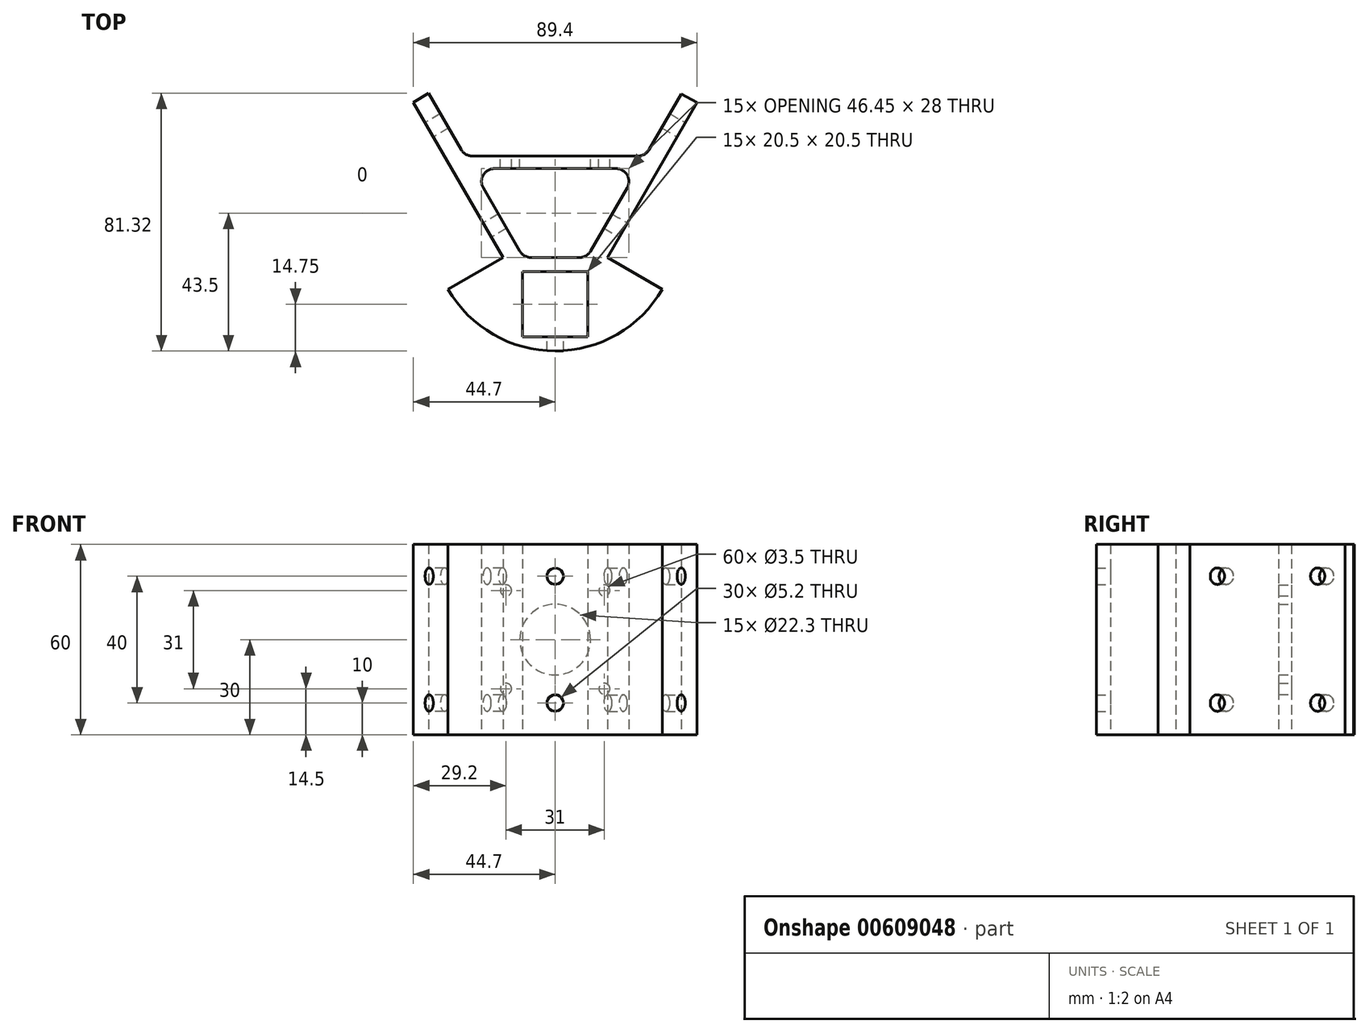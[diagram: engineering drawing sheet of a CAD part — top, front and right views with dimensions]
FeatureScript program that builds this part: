
annotation { "Feature Type Name" : "Feature", "Feature Type Description" : "" }
export const myFeature = defineFeature(function(context is Context, id is Id, definition is map)
    precondition{}
    {
        {
            var Q0;
            Q0=qCreatedBy(makeId("Top.planeOp"),FACE);
            var sketch = newSketch(context, id + "F0", { "sketchPlane" : qUnion([Q0])});
            skArc(sketch, "E0", {"start": v(-33.77, -19.5) * mm, "mid": v(0, -39) * mm, "end": v(33.77, -19.5) * mm});
            skLineSegment(sketch, "E1", {"start": v(16.45, -9.5) * mm, "end": v(44.7, 39.43) * mm});
            skLineSegment(sketch, "E2", {"start": v(-16.45, -9.5) * mm, "end": v(-44.7, 39.43) * mm});
            skLineSegment(sketch, "E3", {"start": v(-33.77, -19.5) * mm, "end": v(-16.45, -9.5) * mm});
            skLineSegment(sketch, "E4", {"start": v(16.45, -9.5) * mm, "end": v(33.77, -19.5) * mm});
            skLineSegment(sketch, "E5", {"start": v(-22.69, 12.5) * mm, "end": v(-11.14, -7.5) * mm});
            skLineSegment(sketch, "E6", {"start": v(22.69, 12.5) * mm, "end": v(11.14, -7.5) * mm});
            skLineSegment(sketch, "E7", {"start": v(-44.7, 39.43) * mm, "end": v(-39.9, 42.32) * mm});
            skLineSegment(sketch, "E8", {"start": v(39.77, 42.08) * mm, "end": v(44.7, 39.43) * mm});
            skLineSegment(sketch, "E9.bottom", {"start": v(10.25, -14) * mm, "end": v(-10.25, -14) * mm});
            skLineSegment(sketch, "E9.top", {"start": v(10.25, -34.5) * mm, "end": v(-10.25, -34.5) * mm});
            skLineSegment(sketch, "E9.left", {"start": v(10.25, -14) * mm, "end": v(10.25, -34.5) * mm});
            skLineSegment(sketch, "E9.right", {"start": v(-10.25, -14) * mm, "end": v(-10.25, -34.5) * mm});
            skPoint(sketch, "E9.middle", {"position": v(0, -24.25) * mm});
            skLineSegment(sketch, "E10", {"start": v(-7.68, -9.5) * mm, "end": v(7.68, -9.5) * mm});
            skLineSegment(sketch, "E11", {"start": v(-19.23, 18.5) * mm, "end": v(19.23, 18.5) * mm});
            skLineSegment(sketch, "E12", {"start": v(-26.15, 22.5) * mm, "end": v(26.15, 22.5) * mm});
            skArc(sketch, "E13.filletArc", {"start": v(-19.23, 18.5) * mm, "mid": v(-22.69, 16.5) * mm, "end": v(-22.69, 12.5) * mm});
            skArc(sketch, "E14.filletArc", {"start": v(22.69, 12.5) * mm, "mid": v(22.69, 16.5) * mm, "end": v(19.23, 18.5) * mm});
            skPoint(sketch, "E15.visualSharp", {"position": v(9.99, -9.5) * mm});
            skArc(sketch, "E15.filletArc", {"start": v(7.68, -9.5) * mm, "mid": v(9.68, -8.96) * mm, "end": v(11.14, -7.5) * mm});
            skPoint(sketch, "E16.visualSharp", {"position": v(-9.99, -9.5) * mm});
            skArc(sketch, "E16.filletArc", {"start": v(-11.14, -7.5) * mm, "mid": v(-9.68, -8.96) * mm, "end": v(-7.68, -9.5) * mm});
            skLineSegment(sketch, "E17", {"start": v(39.77, 42.08) * mm, "end": v(29.62, 24.5) * mm});
            skPoint(sketch, "E18.visualSharp", {"position": v(-28.46, 22.5) * mm});
            skArc(sketch, "E18.filletArc", {"start": v(-29.62, 24.5) * mm, "mid": v(-28.15, 23.04) * mm, "end": v(-26.15, 22.5) * mm});
            skPoint(sketch, "E19.visualSharp", {"position": v(28.46, 22.5) * mm});
            skArc(sketch, "E19.filletArc", {"start": v(26.15, 22.5) * mm, "mid": v(28.15, 23.04) * mm, "end": v(29.62, 24.5) * mm});
            skLineSegment(sketch, "E20", {"start": v(-39.9, 42.32) * mm, "end": v(-29.62, 24.5) * mm});
            skSolve(sketch);
        }
        {
            var Q0;
            Q0=makeQuery(id+"F0.imprint","IMPRINT",FACE,{"disambiguationData":[TD([[makeQuery(id+"F0.imprint","IMPRINT",EDGE,{"derivedFrom":sQuery(id+"F0.wireOp",EDGE,"E0")}),1.0]])]});
            extrude(context, id + "F1", {"entities" : qUnion([Q0]), "depth" : 60 * mm, "offsetDistance" : 25 * mm});
        }
        {
            var Q0;
            Q0=makeQuery(id+"F1.opExtrude","SWEPT_FACE",FACE,{"disambiguationData":[OSD([sQuery(id+"F0.wireOp",EDGE,"E12")])]});
            var sketch = newSketch(context, id + "F2", { "sketchPlane" : qUnion([Q0])});
            skPoint(sketch, "E21", {"position": v(0, 30) * mm});
            skCircle(sketch, "E22", {"center": v(0, 30) * mm, "radius": 11.15 * mm});
            skCircle(sketch, "E23", {"center": v(-15.5, 14.5) * mm, "radius": 1.75 * mm});
            skCircle(sketch, "E24", {"center": v(-15.5, 45.5) * mm, "radius": 1.75 * mm});
            skCircle(sketch, "E25", {"center": v(15.5, 45.5) * mm, "radius": 1.75 * mm});
            skCircle(sketch, "E26", {"center": v(15.5, 14.5) * mm, "radius": 1.75 * mm});
            skPoint(sketch, "E27.3.end.orphan", {"position": v(-26.15, 60) * mm});
            skPoint(sketch, "E27.2.start.orphan", {"position": v(26.15, 60) * mm});
            skPoint(sketch, "E27.1.end.orphan", {"position": v(-26.15, 0) * mm});
            skPoint(sketch, "E27.1.start.orphan", {"position": v(26.15, 0) * mm});
            skSolve(sketch);
        }
        {
            var Q0;
            Q0=makeQuery(id+"F2.imprint","IMPRINT",FACE,{"disambiguationData":[TD([[makeQuery(id+"F2.imprint","IMPRINT",EDGE,{"derivedFrom":sQuery(id+"F2.wireOp",EDGE,"E23")}),1.0]])]});
            var Q1;
            Q1=makeQuery(id+"F2.imprint","IMPRINT",FACE,{"disambiguationData":[TD([[makeQuery(id+"F2.imprint","IMPRINT",EDGE,{"derivedFrom":sQuery(id+"F2.wireOp",EDGE,"E24")}),1.0]])]});
            var Q2;
            Q2=makeQuery(id+"F2.imprint","IMPRINT",FACE,{"disambiguationData":[TD([[makeQuery(id+"F2.imprint","IMPRINT",EDGE,{"derivedFrom":sQuery(id+"F2.wireOp",EDGE,"E25")}),1.0]])]});
            var Q3;
            Q3=makeQuery(id+"F2.imprint","IMPRINT",FACE,{"disambiguationData":[TD([[makeQuery(id+"F2.imprint","IMPRINT",EDGE,{"derivedFrom":sQuery(id+"F2.wireOp",EDGE,"E26")}),1.0]])]});
            var Q4;
            Q4=makeQuery(id+"F2.imprint","IMPRINT",FACE,{"disambiguationData":[TD([[makeQuery(id+"F2.imprint","IMPRINT",EDGE,{"derivedFrom":sQuery(id+"F2.wireOp",EDGE,"E22")}),1.0]])]});
            extrude(context, id + "F3", {"entities" : qUnion([Q0, Q1, Q2, Q3, Q4]), "operationType" : NewBodyOperationType.REMOVE, "oppositeDirection" : true, "depth" : 4 * mm, "offsetDistance" : 25 * mm});
        }
        {
            var Q0;
            Q0=makeQuery(id+"F1.opExtrude","SWEPT_FACE",FACE,{"disambiguationData":[OSD([sQuery(id+"F0.wireOp",EDGE,"E2")])]});
            var sketch = newSketch(context, id + "F4", { "sketchPlane" : qUnion([Q0])});
            skLineSegment(sketch, "E28.0", {"start": v(0, 60) * mm, "end": v(-56.5, 60) * mm});
            skLineSegment(sketch, "E28.1", {"start": v(-56.5, 60) * mm, "end": v(-56.5, 0) * mm});
            skLineSegment(sketch, "E28.2", {"start": v(0, 0) * mm, "end": v(-56.5, 0) * mm});
            skLineSegment(sketch, "E28.3", {"start": v(0, 60) * mm, "end": v(0, 0) * mm});
            skCircle(sketch, "E29", {"center": v(-10, 50) * mm, "radius": 2.6 * mm});
            skCircle(sketch, "E30", {"center": v(-46.5, 50) * mm, "radius": 2.6 * mm});
            skCircle(sketch, "E31", {"center": v(-46.5, 10) * mm, "radius": 2.6 * mm});
            skCircle(sketch, "E32", {"center": v(-10, 10) * mm, "radius": 2.6 * mm});
            skSolve(sketch);
        }
        {
            var Q0;
            Q0=makeQuery(id+"F4.imprint","IMPRINT",FACE,{"disambiguationData":[TD([[makeQuery(id+"F4.imprint","IMPRINT",EDGE,{"derivedFrom":sQuery(id+"F4.wireOp",EDGE,"E30")}),1.0]])]});
            var Q1;
            Q1=makeQuery(id+"F4.imprint","IMPRINT",FACE,{"disambiguationData":[TD([[makeQuery(id+"F4.imprint","IMPRINT",EDGE,{"derivedFrom":sQuery(id+"F4.wireOp",EDGE,"E29")}),1.0]])]});
            var Q2;
            Q2=makeQuery(id+"F4.imprint","IMPRINT",FACE,{"disambiguationData":[TD([[makeQuery(id+"F4.imprint","IMPRINT",EDGE,{"derivedFrom":sQuery(id+"F4.wireOp",EDGE,"E32")}),1.0]])]});
            var Q3;
            Q3=makeQuery(id+"F4.imprint","IMPRINT",FACE,{"disambiguationData":[TD([[makeQuery(id+"F4.imprint","IMPRINT",EDGE,{"derivedFrom":sQuery(id+"F4.wireOp",EDGE,"E31")}),1.0]])]});
            extrude(context, id + "F5", {"entities" : qUnion([Q0, Q1, Q2, Q3]), "operationType" : NewBodyOperationType.REMOVE, "oppositeDirection" : true, "depth" : 5.6 * mm, "offsetDistance" : 25 * mm});
        }
        {
            var Q0;
            Q0=makeQuery(id+"F1.opExtrude","SWEPT_FACE",FACE,{"disambiguationData":[OSD([sQuery(id+"F0.wireOp",EDGE,"E1")])]});
            var sketch = newSketch(context, id + "F6", { "sketchPlane" : qUnion([Q0])});
            skCircle(sketch, "E33", {"center": v(46.5, 50) * mm, "radius": 2.6 * mm});
            skCircle(sketch, "E34", {"center": v(46.5, 10) * mm, "radius": 2.6 * mm});
            skCircle(sketch, "E35", {"center": v(10, 10) * mm, "radius": 2.6 * mm});
            skCircle(sketch, "E36", {"center": v(10, 50) * mm, "radius": 2.6 * mm});
            skSolve(sketch);
        }
        {
            var Q0;
            Q0=makeQuery(id+"F6.imprint","IMPRINT",FACE,{"disambiguationData":[TD([[makeQuery(id+"F6.imprint","IMPRINT",EDGE,{"derivedFrom":sQuery(id+"F6.wireOp",EDGE,"E33")}),1.0]])]});
            var Q1;
            Q1=makeQuery(id+"F6.imprint","IMPRINT",FACE,{"disambiguationData":[TD([[makeQuery(id+"F6.imprint","IMPRINT",EDGE,{"derivedFrom":sQuery(id+"F6.wireOp",EDGE,"E34")}),1.0]])]});
            var Q2;
            Q2=makeQuery(id+"F6.imprint","IMPRINT",FACE,{"disambiguationData":[TD([[makeQuery(id+"F6.imprint","IMPRINT",EDGE,{"derivedFrom":sQuery(id+"F6.wireOp",EDGE,"E35")}),1.0]])]});
            var Q3;
            Q3=makeQuery(id+"F6.imprint","IMPRINT",FACE,{"disambiguationData":[TD([[makeQuery(id+"F6.imprint","IMPRINT",EDGE,{"derivedFrom":sQuery(id+"F6.wireOp",EDGE,"E36")}),1.0]])]});
            extrude(context, id + "F7", {"entities" : qUnion([Q0, Q1, Q2, Q3]), "operationType" : NewBodyOperationType.REMOVE, "oppositeDirection" : true, "depth" : 5.6 * mm, "offsetDistance" : 25 * mm});
        }
        {
            var Q0;
            Q0=makeQuery(id+"F1.opExtrude","SWEPT_FACE",FACE,{"disambiguationData":[OSD([sQuery(id+"F0.wireOp",EDGE,"E9.top")])]});
            var sketch = newSketch(context, id + "F8", { "sketchPlane" : qUnion([Q0])});
            skCircle(sketch, "E37", {"center": v(0, 10) * mm, "radius": 2.6 * mm});
            skCircle(sketch, "E38", {"center": v(0, 50) * mm, "radius": 2.6 * mm});
            skSolve(sketch);
        }
        {
            var Q0;
            Q0=makeQuery(id+"F8.imprint","IMPRINT",FACE,{"disambiguationData":[TD([[makeQuery(id+"F8.imprint","IMPRINT",EDGE,{"derivedFrom":sQuery(id+"F8.wireOp",EDGE,"E38")}),1.0]])]});
            var Q1;
            Q1=makeQuery(id+"F8.imprint","IMPRINT",FACE,{"disambiguationData":[TD([[makeQuery(id+"F8.imprint","IMPRINT",EDGE,{"derivedFrom":sQuery(id+"F8.wireOp",EDGE,"E37")}),1.0]])]});
            extrude(context, id + "F9", {"entities" : qUnion([Q0, Q1]), "operationType" : NewBodyOperationType.REMOVE, "endBound" : BoundingType.THROUGH_ALL, "oppositeDirection" : true, "depth" : 4 * mm, "offsetDistance" : 25 * mm});
        }
    });
